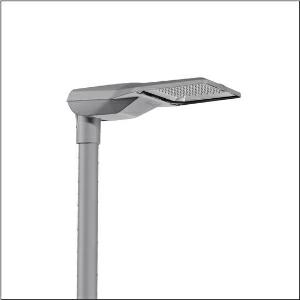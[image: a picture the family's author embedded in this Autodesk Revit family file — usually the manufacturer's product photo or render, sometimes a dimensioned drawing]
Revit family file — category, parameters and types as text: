
# Revit family: streetlight_sl_21_iq_midi___st0_8a_5xe3c41g08nb_9f8f
name_source: partatom
category: Lighting Fixtures
units: mm (PartAtom-declared; Revit-internal decimal feet)

## family parameters
Cut with Voids When Loaded = No
Host = Face
Light Source = No
Part Type = Normal
Room Calculation Point = No
Round Connector Dimension = Use Diameter
Shared = No

## types (1)
- --- (1 x LED, 24250 lm, 155.5 W, 4000K)
    Apparent Load = 155 VA
    CIE Flux Codes = 41 75 97 100 100
    Color Rendering = 70
    Color Temperature = 4000K
    Default Elevation = 1800 mm
    Description = Streetlight SL 21 iQ midi, mast luminaire, primary light control with lens, of PMMA, primary optical cover: cover, of toughened safety glass, transparent, light distribution: ST0.8a, light emission: direct distribution, primary light characteristic: asymmetric, installation type: post-top, side-entry, LED, High Power LED, rated luminous flux: 24.250lm, luminous efficacy: 156lm/W, light colour: 740, colour temperature: 4000K, control: Street-Remote, Auto-Match, Temp-Guard, Lumen-Switch, Night-Set, Smart-Wire, Light-Fading, Desk-Remote (wireless, voltage-free reading and setting of iQ features in the workshop via application-optimized NFC function/RFID function), optimised constant luminous flux control (CLO 2.0), pre-setting: linear dimming characteristic, mains connection: 230..240V, AC, 50/60Hz, start of lifetime: 156W, end of service life: 162W, reduction: 69W, luminaire housing, of diecast aluminium, powder-coated, Siteco® metallic grey (DB 702S), corrosivity category C5 mid according to DIN EN ISO 12944, please order mast flange separately, inclination adjustable: 0°, 5°, 10°, 15°, sealing non-destructively replaceable, multi-level sealing system, length: 644mm, width: 335mm, height: 110mm, mast flange for spigot size: 42mm (side-entry): 5XC10008XM4, 60/48mm (side-entry/post-top): 5XC10108XM2, 76/60mm (side-entry/post-top): 5XC10108XM1, protection rating (complete): IP66, insulation class (complete): insulation class II (safety insulation), certification: CE, ENEC, ENEC+, VDE, impact resistance: IK09, permissible operating ambient temperature for outdoor applications: -40..+50°C, standard-compliant lighting for roads and squares, packaging unit: 1 piece

Light Distribution: ST0.8a
    Height = 111 mm
    Lamp = 1 x LED
    Lamp Light Flux = 24250 lm
    Lamp Power = 155.5 W
    Lamp count = 1
    Length = 644 mm
    Luminous efficacy = 156 lm/W
    Manufacturer = Siteco
    ModVariant = No
    Model = 5XE3C41G08NB
    Number of Poles = 1
    OnlyDefault = Yes
    Power Factor = 1
    Product Name = Streetlight SL 21 iQ midi | ST0.8a
    Product group = mast luminaire | pylon top
    ProductGroupID = 6100
    Protection Class = Protection class II
    Protection Degree = IP 66
    RLX_Detail_Level = 1
    RLX_Emergency_Light_Flux = 0 lm
    RLX_Emergency_Type = 0
    RLX_Emergency_Type_DB = No
    RlxData = <blob elided: 90705 chars, md5=74c59b8f>
    Socket = socket
    Standby Power = 0 W
    System Light Flux = 24250 lm
    System Power = 155 W
    Type Comments = factory setting: luminous flux: 100 % | dim-lin: 254 | 823 mA
    Type Image = l_1004298.jpg
    URL = http://relux.com
    VarID = @adj_139339
    Voltage = 0 V
    Weight = 0.00 kg
    Width = 336 mm

## geometry (parser evidence)
native form markers: Blend x4, Sweep x10
no freeform markers — native parametric forms only
